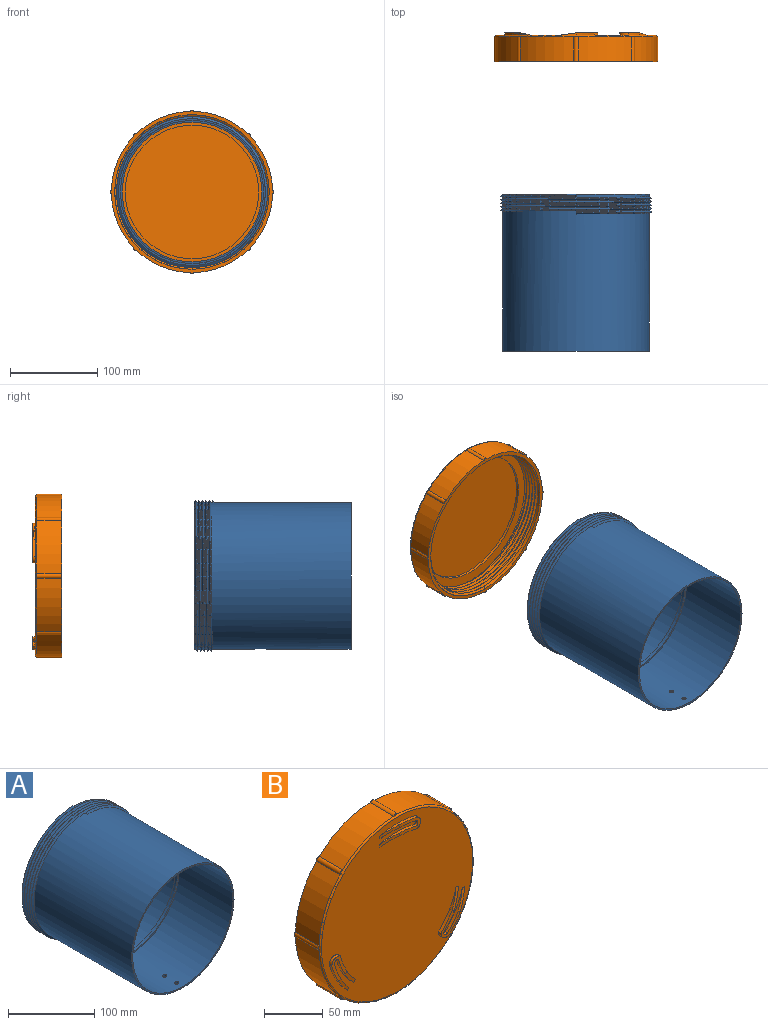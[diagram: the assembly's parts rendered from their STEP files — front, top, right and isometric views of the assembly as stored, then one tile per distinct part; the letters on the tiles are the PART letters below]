
ASSEMBLY  parts=2 mates=1
PART A: 20 faces, bbox 199.8x180x173 mm
  f0: cylinder r=84mm len=168mm, axis (0,1,0), area 83625.4mm2, adj f5,f8,f14,f15,f17,f18,f19
  f1: cylinder r=84mm len=168mm, axis (0,1,0), area 1055.6mm2, adj f2,f9,f13,f16
  f2: cylinder r=84mm len=168mm, axis (0,1,0), area 587.6mm2, adj f1,f3,f15,f16
  f3: cylinder r=84mm len=168mm, axis (0,1,0), area 587.6mm2, adj f2,f4,f15,f16
  f4: cylinder r=84mm len=168mm, axis (0,1,0), area 587.6mm2, adj f3,f5,f15,f16
  f5: cylinder r=84mm len=168mm, axis (0,1,0), area 587.6mm2, adj f0,f4,f15,f16
  f6: cylinder r=82mm len=164mm, axis (0,1,0), area 45300.5mm2, adj f8,f10,f18,f19
  f7: cylinder r=82mm len=164mm, axis (0,1,0), area 45025.2mm2, adj f9,f11,f17
  f8: plane 168x168mm, normal (0,-1,0), area 1043mm2, adj f0,f6
  f9: plane 168x168mm, normal (0,1,0), area 1043mm2, adj f1,f7
  f10: plane 164x164mm, normal (0,-1,0), area 1017.9mm2, adj f6,f12
  f11: plane 164x164mm, normal (0,1,0), area 1017.9mm2, adj f7,f12
  f12: cylinder r=80mm len=160mm, axis (0,1,0), area 2010.6mm2, adj f10,f11
  f13: plane 2.89x2.5mm, normal (1,0,0), area 3.6mm2, adj f1,f15,f16
  f14: plane 2.89x2.5mm, normal (-1,0,0), area 3.6mm2, adj f0,f15,f16
  f15: bspline ~199.76x173mm, area 7725.5mm2, adj f0,f2,f3,f4,f5,f13,f14,f16
  f16: bspline ~199.76x173mm, area 7731.3mm2, adj f1,f2,f3,f4,f5,f13,f14,f15
  f17: cylinder r=10mm len=20mm, axis (0,0,1), area 126.1mm2, adj f0,f7
  f18: cylinder r=2.5mm len=5mm, axis (0,0,1), area 31.4mm2, adj f0,f6
  f19: cylinder r=2.5mm len=5mm, axis (0,0,1), area 31.4mm2, adj f0,f6
PART B: 73 faces, bbox 207x35.6x202.9 mm
  f0: plane 182.02x182.02mm, normal (0,-1,0), area 25153.1mm2, adj f14,f35,f36,f37,f40,f41,f42,f43
  f1: cylinder r=92.5mm len=61.25mm, axis (0,1,0), area 1932.3mm2, adj f10,f14,f30,f32
  f2: cylinder r=92.5mm len=61.25mm, axis (0,1,0), area 1932.3mm2, adj f10,f14,f18,f32
  f3: cylinder r=92.5mm len=61.25mm, axis (0,1,0), area 1932.3mm2, adj f10,f14,f28,f30
  f4: cylinder r=92.5mm len=61.25mm, axis (0,1,0), area 1932.3mm2, adj f10,f14,f26,f28
  f5: cylinder r=92.5mm len=61.25mm, axis (0,1,0), area 1932.3mm2, adj f10,f14,f24,f26
  f6: cylinder r=92.5mm len=61.25mm, axis (0,1,0), area 1932.3mm2, adj f10,f14,f22,f24
  f7: cylinder r=92.5mm len=61.25mm, axis (0,1,0), area 1932.3mm2, adj f10,f14,f20,f22
  f8: cylinder r=92.5mm len=61.25mm, axis (0,1,0), area 1932.3mm2, adj f10,f14,f18,f20
  f9: cylinder r=88.5mm len=177mm, axis (0,1,0), area 5330.2mm2, adj f10,f11,f15,f16,f17
  f10: plane 187.4x187.4mm, normal (0,1,0), area 2307.2mm2, adj f1,f2,f3,f4,f5,f6,f7,f8
  f11: plane 178.62x177.65mm, normal (0,1,0), area 5788.2mm2, adj f9,f12,f16,f17
  f12: cylinder r=76.5mm len=153mm, axis (0,1,0), area 1442mm2, adj f11,f13
  f13: plane 153x153mm, normal (0,1,0), area 18385.4mm2, adj f12
  f14: torus R=91mm, axis (0,-1,0), area 1361.3mm2, adj f0,f1,f2,f3,f4,f5,f6,f7
  f15: plane 2.89x2.5mm, normal (1,0,0), area 3.6mm2, adj f9,f16,f17
  f16: bspline ~204.38x177mm, area 7672.4mm2, adj f9,f11,f15,f17
  f17: bspline ~204.38x177mm, area 7173.2mm2, adj f9,f11,f15,f16
  f18: cylinder r=3mm len=28.5mm, axis (0,1,0), area 161mm2, adj f2,f8,f10,f19
  f19: plane 4.85x1.23mm, normal (0,-1,0), area 4.1mm2, adj f14,f18
  f20: cylinder r=3mm len=28.5mm, axis (0,1,0), area 161mm2, adj f7,f8,f10,f21
  f21: plane 3.47x3.47mm, normal (0,-1,0), area 4.1mm2, adj f14,f20
  f22: cylinder r=3mm len=28.5mm, axis (0,1,0), area 161mm2, adj f6,f7,f10,f23
  f23: plane 4.85x1.23mm, normal (0,-1,0), area 4.1mm2, adj f14,f22
  f24: cylinder r=3mm len=28.5mm, axis (0,1,0), area 161mm2, adj f5,f6,f10,f25
  f25: plane 3.47x3.47mm, normal (0,-1,0), area 4.1mm2, adj f14,f24
  f26: cylinder r=3mm len=28.5mm, axis (0,1,0), area 161mm2, adj f4,f5,f10,f27
  f27: plane 4.85x1.23mm, normal (0,-1,0), area 4.1mm2, adj f14,f26
  f28: cylinder r=3mm len=28.5mm, axis (0,1,0), area 161mm2, adj f3,f4,f10,f29
  f29: plane 3.47x3.47mm, normal (0,-1,0), area 4.1mm2, adj f14,f28
  f30: cylinder r=3mm len=28.5mm, axis (0,1,0), area 161mm2, adj f1,f3,f10,f31
  f31: plane 4.85x1.23mm, normal (0,-1,0), area 4.1mm2, adj f14,f30
  f32: cylinder r=3mm len=28.5mm, axis (0,1,0), area 161mm2, adj f1,f2,f10,f33
  f33: plane 3.47x3.47mm, normal (0,-1,0), area 4.1mm2, adj f14,f32
  f34: plane 25.24x14.65mm, normal (0,-1,0), area 160mm2, adj f35,f36,f37,f38,f39,f40,f41,f42
  f35: cylinder r=84.5mm len=21.38mm, axis (0,-1,0), area 32.5mm2, adj f0,f34,f37,f44
  f36: cylinder r=81.5mm len=41.06mm, axis (0,-1,0), area 92.2mm2, adj f0,f34,f37,f38,f42
  f37: plane 21.4x5.68mm, normal (-0.13,-0.99,-0.04), area 64.3mm2, adj f0,f34,f35,f36,f38
  f38: plane 2.87x0.1mm, normal (-1,0,0), area 0.1mm2, adj f34,f36,f37
  f39: plane 2.73x0.11mm, normal (-1,0,0), area 0.1mm2, adj f34,f41,f46
  f40: cylinder r=76mm len=42.19mm, axis (0,-1,0), area 95.8mm2, adj f0,f34,f42,f46
  f41: bspline ~21.32x3.18mm, area 64.4mm2, adj f0,f34,f39,f43,f45
  f42: cylinder r=3.5mm len=5.79mm, axis (0,1,0), area 20.5mm2, adj f0,f34,f36,f40
  f43: bspline ~11.97x4.12mm, area 44.5mm2, adj f0,f34,f41,f44
  f44: bspline ~21.66x3mm, area 65.4mm2, adj f0,f34,f35,f43
  f45: cylinder r=73mm len=20.58mm, axis (0,-1,0), area 30.2mm2, adj f0,f41,f46
  f46: plane 21.45x5.99mm, normal (-0.13,-0.99,-0.04), area 64.5mm2, adj f0,f34,f39,f40,f45
  f47: plane 27.01x18.36mm, normal (0,-1,0), area 160mm2, adj f48,f49,f50,f51,f52,f53,f54,f55
  f48: cylinder r=84.5mm len=17.14mm, axis (0,-1,0), area 32.5mm2, adj f0,f47,f50,f57
  f49: cylinder r=81.5mm len=35.53mm, axis (0,-1,0), area 92.2mm2, adj f0,f47,f50,f51,f55
  f50: plane 18.67x15.21mm, normal (0.1,-0.99,-0.1), area 64.3mm2, adj f0,f47,f48,f49,f51
  f51: plane 2.48x1.43mm, normal (0.5,0,-0.87), area 0.1mm2, adj f47,f49,f50
  f52: plane 2.36x1.36mm, normal (0.5,0,-0.87), area 0.1mm2, adj f47,f54,f59
  f53: cylinder r=76mm len=36.44mm, axis (0,-1,0), area 95.8mm2, adj f0,f47,f55,f59
  f54: bspline ~20.05x7.91mm, area 64.4mm2, adj f0,f47,f52,f56,f58
  f55: cylinder r=3.5mm len=4.85mm, axis (0,1,0), area 20.5mm2, adj f0,f47,f49,f53
  f56: bspline ~10.59x7.03mm, area 44.5mm2, adj f0,f47,f54,f57
  f57: bspline ~20.17x8.39mm, area 65.4mm2, adj f0,f47,f48,f56
  f58: cylinder r=73mm len=16.34mm, axis (0,-1,0), area 30.2mm2, adj f0,f54,f59
  f59: plane 18.54x15.44mm, normal (0.1,-0.99,-0.1), area 64.5mm2, adj f0,f47,f52,f53,f58
  f60: plane 24.12x23.33mm, normal (0,-1,0), area 160mm2, adj f61,f62,f63,f64,f65,f66,f67,f68
  f61: cylinder r=84.5mm len=19.89mm, axis (0,-1,0), area 32.5mm2, adj f0,f60,f63,f70
  f62: cylinder r=81.5mm len=35.58mm, axis (0,-1,0), area 92.2mm2, adj f0,f60,f63,f64,f68
  f63: plane 20.68x10.93mm, normal (0.04,-0.99,0.13), area 64.3mm2, adj f0,f60,f61,f62,f64
  f64: plane 2.48x1.43mm, normal (0.5,0,0.87), area 0.1mm2, adj f60,f62,f63
  f65: plane 2.36x1.36mm, normal (0.5,0,0.87), area 0.1mm2, adj f60,f67,f72
  f66: cylinder r=76mm len=36.63mm, axis (0,-1,0), area 95.8mm2, adj f0,f60,f68,f72
  f67: bspline ~16.88x13.41mm, area 64.4mm2, adj f0,f60,f65,f69,f71
  f68: cylinder r=3.5mm len=5.18mm, axis (0,1,0), area 20.5mm2, adj f0,f60,f62,f66
  f69: bspline ~10.19x7.51mm, area 44.5mm2, adj f0,f60,f67,f70
  f70: bspline ~17.35x13.28mm, area 65.4mm2, adj f0,f60,f61,f69
  f71: cylinder r=73mm len=19.3mm, axis (0,-1,0), area 30.2mm2, adj f0,f67,f72
  f72: plane 20.76x10.67mm, normal (0.03,-0.99,0.14), area 64.5mm2, adj f0,f60,f65,f66,f71
PLACE A t=(-149.03,-20.17,-21.22)mm
PLACE B rot(axis=(1,0,0),180deg) t=(-149.03,131.83,-21.22)mm
MATE fastened B.f1 <-> A.f0  axis (0,-1,0) through (-149.03,154.83,-21.22)mm
